# Revit family: LT573
name_source: partatom
category: Plumbing Fixtures
revit_build: Autodesk Revit 2014 (Build: 20130308_1515(x64)
units: mm (PartAtom-declared; Revit-internal decimal feet)

## types (1)
- LT573
    Codes/Standards = • Meets ADA guidelines and ANSI A117.1
requirements when countertop is installed 864mm
(34") from finished floor and lavatory is installed
79mm (3-1/8") minimum from front edge.
• Meets and exceeds ASME A112.19.2/CSA B45.1
• Certifications: IAPMO(cUPC), State of
Massachusetts , City of Los Angeles, and others
• Code compliance: UPC, IPC, NSPC, NPC Canada,
and others
• ADA compliant
    Colors/Finishes = Standard #01 Cotton
    Manufacturer = TOTO USA
    Model = LT573
    Specifications = • Waste 1-1/4" (32 mm)
• Size 16-9/16" (420 mm)
• Basin 16-1/8" (409 mm)
• Basin Depth 4-1/8" (105 mm)
• Warranty One Year Limited Warranty
• Material Vitreous China
• Shipping Weight 19 lbs.
• Shipping Dimensions 17-3/4" x 17-3/4" x 7-3/4"
    sink = Polypropylene
    steel = Steel, Galvanized

## geometry (parser evidence)
native form markers: Sweep x5
no freeform markers — native parametric forms only
